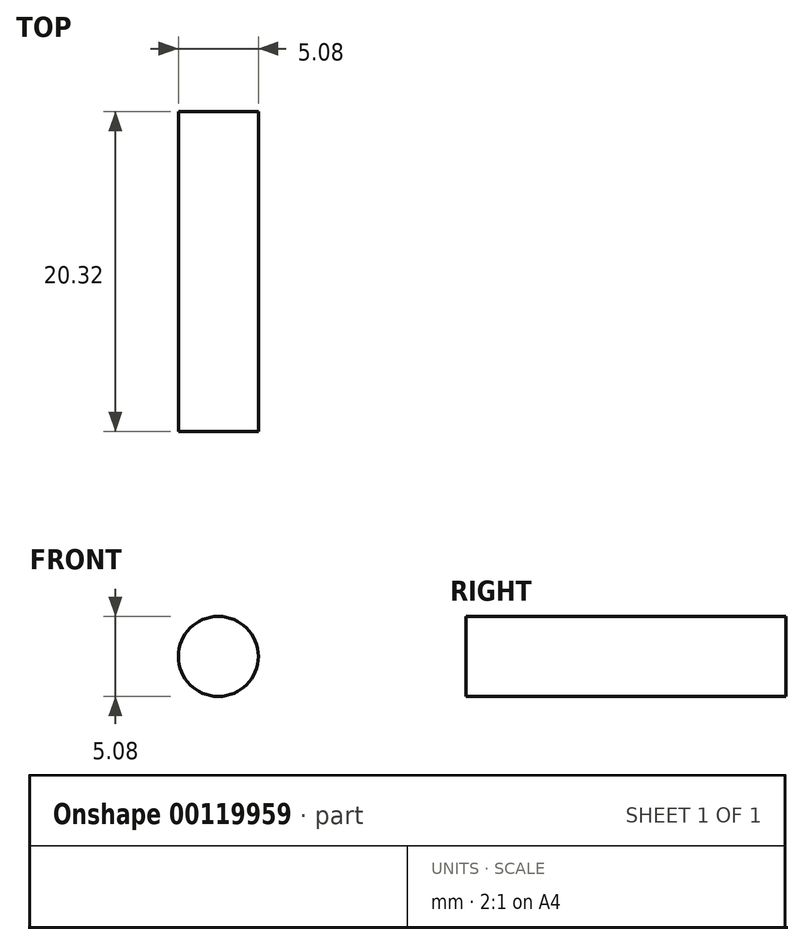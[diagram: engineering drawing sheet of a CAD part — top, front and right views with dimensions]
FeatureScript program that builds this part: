
annotation { "Feature Type Name" : "Feature", "Feature Type Description" : "" }
export const myFeature = defineFeature(function(context is Context, id is Id, definition is map)
    precondition{}
    {
        {
            var Q0;
            Q0=qCreatedBy(makeId("Front.planeOp"),FACE);
            var sketch = newSketch(context, id + "F0", { "sketchPlane" : qUnion([Q0])});
            skCircle(sketch, "E0", {"center": v(0, 0) * mm, "radius": 2.54 * mm});
            skSolve(sketch);
        }
        {
            var Q0;
            Q0=makeQuery(id+"F0.imprint","IMPRINT",FACE,{"disambiguationData":[TD([[makeQuery(id+"F0.imprint","IMPRINT",EDGE,{"derivedFrom":sQuery(id+"F0.wireOp",EDGE,"E0")}),1.0]])]});
            extrude(context, id + "F1", {"entities" : qUnion([Q0]), "depth" : 20.32 * mm});
        }
    });
